# Revit family: Toilet_Elongated-American_Standard-Cadet_PRO-215CB_Series
name_source: partatom
category: Plumbing Fixtures
revit_build: Autodesk Revit 2014 (Build: 20130308_1515(x64)
units: mm (PartAtom-declared; Revit-internal decimal feet)

## types (2) — shared parameters
Assembly Code = D2010110
Bowl Shape = Elongated
CW Connection = Yes
CWFU = 5
Cold Water Connection Diameter = 1/4"
Cold Water Connection Height = 8"
Cold Water Connection Radius = 1/8"
Default Elevation = 0"
Description = Cadet PRO Elongated Toilet 10" Rough-In.
HW Connection = No
Height = 28 7/8"
Installation Type = Floor mounted
Length = 30 1/8"
Manufacturer = American Standard
Material = Vitreous China-American Standard-020-White
Price = Prices may vary. Please consult Manufacturer Representative for most up-to-date price list.
Product Documentation Link = https://www.americanstandard-us.com
Product Page URL = https://www.americanstandard-us.com
Revised Date = 01/17/2017
URL = http://www.americanstandard-us.com
Vent Connection = No
WFU = 5
Warranty Information = 5 Year Limited
Waste Connection = Yes
Waste Connection Diameter = 2 1/8"
Waste Connection Radius = 1 1/16"
Width = 18 1/8"
zero-valued in all types: HWFU

## per-type parameters (varying)
| type | Flush Rate |
| 215CB.004 | (6.0 Lpf/1.6gpf) |
| 215CB.104 | (4.8 Lpf/1.28gpf) |

note: column(s) folded — value = type name in every type: Model

## geometry (parser evidence)
native form markers: Sweep x1
no freeform markers — native parametric forms only
